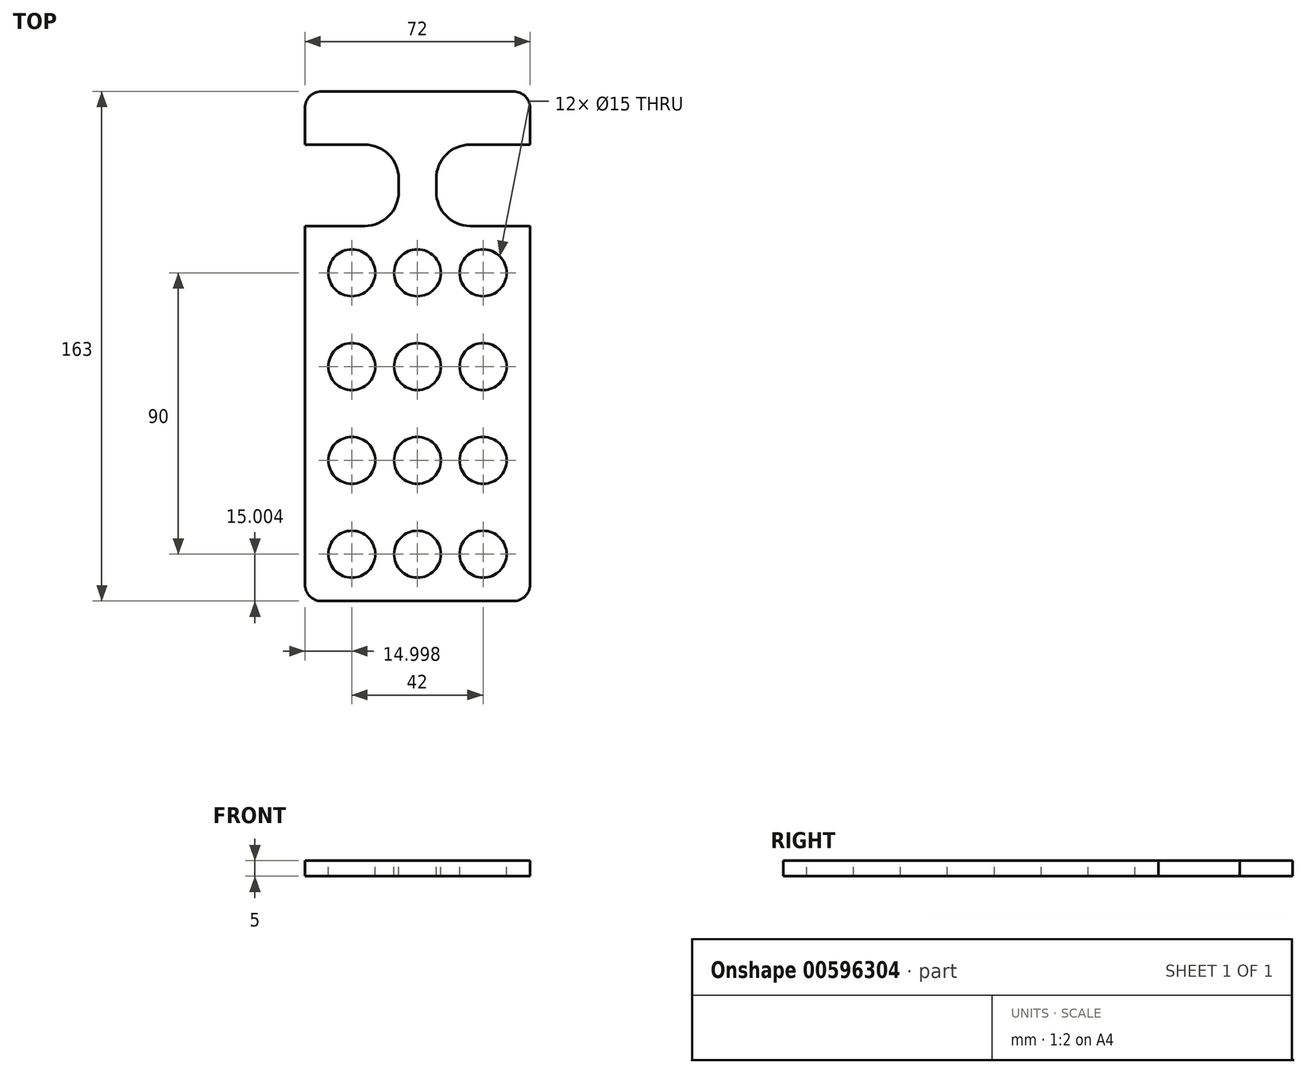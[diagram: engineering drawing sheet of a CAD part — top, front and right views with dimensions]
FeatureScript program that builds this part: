
annotation { "Feature Type Name" : "Feature", "Feature Type Description" : "" }
export const myFeature = defineFeature(function(context is Context, id is Id, definition is map)
    precondition{}
    {
        {
            var Q0;
            Q0=qCreatedBy(makeId("Top.planeOp"),FACE);
            var sketch = newSketch(context, id + "F0", { "sketchPlane" : qUnion([Q0])});
            skLineSegment(sketch, "E0.bottom", {"start": v(-44.34, 126.57) * mm, "end": v(27.66, 126.57) * mm});
            skLineSegment(sketch, "E0.top", {"start": v(-44.34, -36.43) * mm, "end": v(27.66, -36.43) * mm});
            skLineSegment(sketch, "E0.left", {"start": v(-44.34, 126.57) * mm, "end": v(-44.34, -36.43) * mm});
            skLineSegment(sketch, "E0.right", {"start": v(27.66, 126.57) * mm, "end": v(27.66, -36.43) * mm});
            skSolve(sketch);
        }
        {
            var Q0;
            Q0 = qSketchRegion(id + "F0", true);
            extrude(context, id + "F1", {"entities" : qUnion([Q0]), "oppositeDirection" : true, "depth" : 5 * mm, "offsetDistance" : 25 * mm});
        }
        {
            var Q0;
            Q0=makeQuery(id+"F0.imprint","IMPRINT",FACE,{"disambiguationData":[TD([[makeQuery(id+"F0.imprint","IMPRINT",EDGE,{"derivedFrom":sQuery(id+"F0.wireOp",EDGE,"E0.bottom")}),-1.0]])]});
            var sketch = newSketch(context, id + "F2", { "sketchPlane" : qUnion([Q0])});
            skLineSegment(sketch, "E1.bottom", {"start": v(27.66, 109.57) * mm, "end": v(-2.34, 109.57) * mm});
            skLineSegment(sketch, "E1.top", {"start": v(27.66, 83.57) * mm, "end": v(-2.34, 83.57) * mm});
            skLineSegment(sketch, "E1.left", {"start": v(27.66, 109.57) * mm, "end": v(27.66, 83.57) * mm});
            skLineSegment(sketch, "E1.right", {"start": v(-2.34, 109.57) * mm, "end": v(-2.34, 83.57) * mm});
            skLineSegment(sketch, "E2.bottom", {"start": v(-44.34, 109.57) * mm, "end": v(-14.34, 109.57) * mm});
            skLineSegment(sketch, "E2.top", {"start": v(-44.34, 83.57) * mm, "end": v(-14.34, 83.57) * mm});
            skLineSegment(sketch, "E2.left", {"start": v(-44.34, 109.57) * mm, "end": v(-44.34, 83.57) * mm});
            skLineSegment(sketch, "E2.right", {"start": v(-14.34, 109.57) * mm, "end": v(-14.34, 83.57) * mm});
            skCircle(sketch, "E3", {"center": v(12.66, 68.57) * mm, "radius": 7.5 * mm});
            skCircle(sketch, "E4", {"center": v(-29.34, 68.57) * mm, "radius": 7.5 * mm});
            skCircle(sketch, "E5", {"center": v(-8.34, 38.57) * mm, "radius": 7.5 * mm});
            skCircle(sketch, "E6", {"center": v(-29.34, -21.43) * mm, "radius": 7.5 * mm});
            skCircle(sketch, "E7", {"center": v(12.66, -21.43) * mm, "radius": 7.5 * mm});
            skCircle(sketch, "E8", {"center": v(12.66, 38.57) * mm, "radius": 7.5 * mm});
            skCircle(sketch, "E9", {"center": v(-8.34, 68.57) * mm, "radius": 7.5 * mm});
            skCircle(sketch, "E10", {"center": v(-29.34, 38.57) * mm, "radius": 7.5 * mm});
            skCircle(sketch, "E11", {"center": v(-8.34, -21.43) * mm, "radius": 7.5 * mm});
            skCircle(sketch, "E12", {"center": v(-29.34, 8.57) * mm, "radius": 7.5 * mm});
            skCircle(sketch, "E13", {"center": v(12.66, 8.57) * mm, "radius": 7.5 * mm});
            skCircle(sketch, "E14", {"center": v(-8.34, 8.57) * mm, "radius": 7.5 * mm});
            skSolve(sketch);
        }
        {
            var Q0;
            Q0 = qSketchRegion(id + "F2", true);
            extrude(context, id + "F3", {"entities" : qUnion([Q0]), "operationType" : NewBodyOperationType.REMOVE, "oppositeDirection" : true, "depth" : 25 * mm, "offsetDistance" : 25 * mm});
        }
        {
            var Q0;
            Q0=makeQuery(id+"F3.boolean.opBoolean","COPY",EDGE,{"derivedFrom":makeQuery(id+"F3.opExtrude","SWEPT_EDGE",EDGE,{"disambiguationData":[OSD([sQuery(id+"F2.wireOp",EDGE,"E1.bottom"),sQuery(id+"F2.wireOp",EDGE,"E1.right")])]})});
            var Q1;
            Q1=makeQuery(id+"F3.boolean.opBoolean","COPY",EDGE,{"derivedFrom":makeQuery(id+"F3.opExtrude","SWEPT_EDGE",EDGE,{"disambiguationData":[OSD([sQuery(id+"F2.wireOp",EDGE,"E1.top"),sQuery(id+"F2.wireOp",EDGE,"E1.right")])]})});
            var Q2;
            Q2=makeQuery(id+"F3.boolean.opBoolean","COPY",EDGE,{"derivedFrom":makeQuery(id+"F3.opExtrude","SWEPT_EDGE",EDGE,{"disambiguationData":[OSD([sQuery(id+"F2.wireOp",EDGE,"E2.top"),sQuery(id+"F2.wireOp",EDGE,"E2.right")])]})});
            var Q3;
            Q3=makeQuery(id+"F3.boolean.opBoolean","COPY",EDGE,{"derivedFrom":makeQuery(id+"F3.opExtrude","SWEPT_EDGE",EDGE,{"disambiguationData":[OSD([sQuery(id+"F2.wireOp",EDGE,"E2.bottom"),sQuery(id+"F2.wireOp",EDGE,"E2.right")])]})});
            fillet(context, id + "F4", {"entities" : qUnion([Q0, Q1, Q2, Q3]), "radius" : 10.86 * mm, "tangentPropagation" : true, "allowEdgeOverflow" : false});
        }
        {
            var Q0;
            Q0=makeQuery(id+"F1.opExtrude","SWEPT_EDGE",EDGE,{"disambiguationData":[OSD([sQuery(id+"F0.wireOp",EDGE,"E0.bottom"),sQuery(id+"F0.wireOp",EDGE,"E0.right")])]});
            var Q1;
            Q1=makeQuery(id+"F1.opExtrude","SWEPT_EDGE",EDGE,{"disambiguationData":[OSD([sQuery(id+"F0.wireOp",EDGE,"E0.bottom"),sQuery(id+"F0.wireOp",EDGE,"E0.left")])]});
            var Q2;
            Q2=makeQuery(id+"F3.boolean.opBoolean","COPY",EDGE,{"derivedFrom":makeQuery(id+"F3.opExtrude","SWEPT_EDGE",EDGE,{"disambiguationData":[OSD([sQuery(id+"F0.wireOp",EDGE,"E0.left"),sQuery(id+"F2.wireOp",EDGE,"E2.bottom"),sQuery(id+"F2.wireOp",EDGE,"E2.left")])]})});
            var Q3;
            Q3=makeQuery(id+"F3.boolean.opBoolean","COPY",EDGE,{"derivedFrom":makeQuery(id+"F3.opExtrude","SWEPT_EDGE",EDGE,{"disambiguationData":[OSD([sQuery(id+"F0.wireOp",EDGE,"E0.left"),sQuery(id+"F2.wireOp",EDGE,"E2.top"),sQuery(id+"F2.wireOp",EDGE,"E2.left")])]})});
            var Q4;
            Q4=makeQuery(id+"F3.boolean.opBoolean","COPY",EDGE,{"derivedFrom":makeQuery(id+"F3.opExtrude","SWEPT_EDGE",EDGE,{"disambiguationData":[OSD([sQuery(id+"F0.wireOp",EDGE,"E0.right"),sQuery(id+"F2.wireOp",EDGE,"E1.bottom"),sQuery(id+"F2.wireOp",EDGE,"E1.left")])]})});
            var Q5;
            Q5=makeQuery(id+"F3.boolean.opBoolean","COPY",EDGE,{"derivedFrom":makeQuery(id+"F3.opExtrude","SWEPT_EDGE",EDGE,{"disambiguationData":[OSD([sQuery(id+"F0.wireOp",EDGE,"E0.right"),sQuery(id+"F2.wireOp",EDGE,"E1.top"),sQuery(id+"F2.wireOp",EDGE,"E1.left")])]})});
            var Q6;
            Q6=makeQuery(id+"F1.opExtrude","SWEPT_EDGE",EDGE,{"disambiguationData":[OSD([sQuery(id+"F0.wireOp",EDGE,"E0.top"),sQuery(id+"F0.wireOp",EDGE,"E0.left")])]});
            var Q7;
            Q7=makeQuery(id+"F1.opExtrude","SWEPT_EDGE",EDGE,{"disambiguationData":[OSD([sQuery(id+"F0.wireOp",EDGE,"E0.top"),sQuery(id+"F0.wireOp",EDGE,"E0.right")])]});
            fillet(context, id + "F5", {"entities" : qUnion([Q0, Q1, Q2, Q3, Q4, Q5, Q6, Q7]), "radius" : 5.3 * mm, "tangentPropagation" : true, "allowEdgeOverflow" : false});
        }
    });
